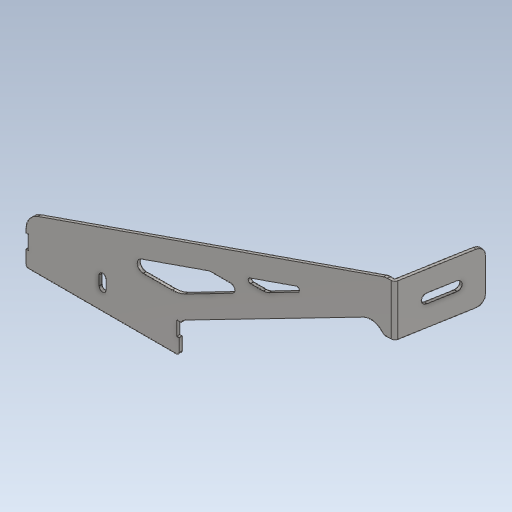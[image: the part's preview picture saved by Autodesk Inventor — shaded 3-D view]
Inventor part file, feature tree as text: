
AUTODESK INVENTOR PART (.ipt)
format: ipt  version: 2020 (Build 240168000, 168)  size: 419,328 bytes
history: native  units: mm
features: other x3, extrude x1, plane x1
ambient origin geometry x8: Origin, YZ Plane, XZ Plane, XY Plane, X Axis, Y Axis, Z Axis, Center Point
bodies: Body1 (feature_tree)
feature tree (5):
  other  "實體1"
  extrude  "擠出1"  Depth=130.0mm
  other  "折彎零件1"
  plane  "工作平面1"
  other  "定義1"
